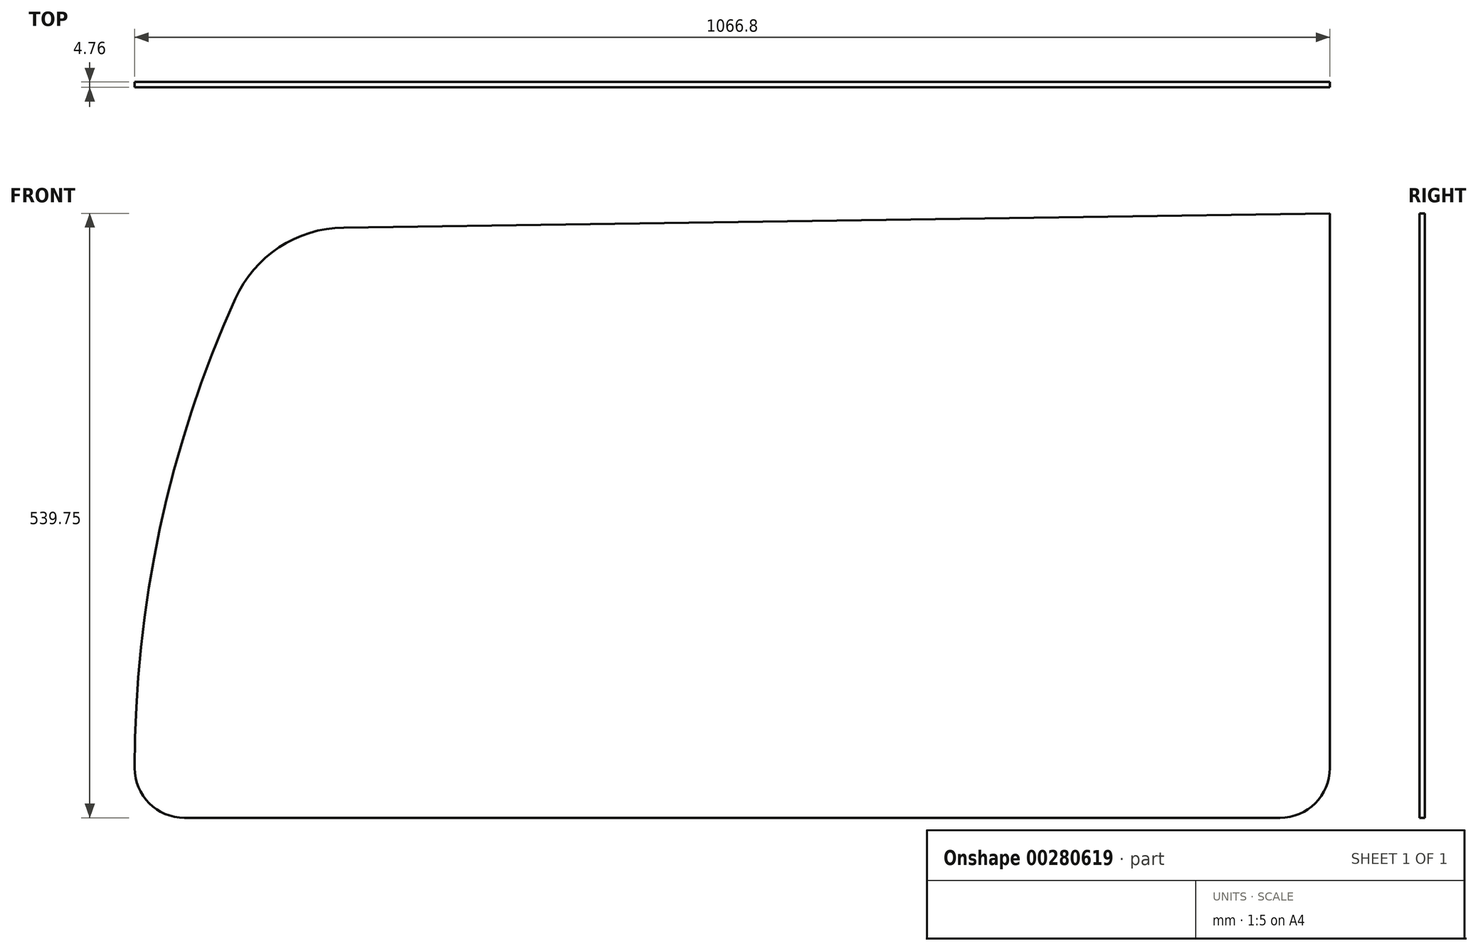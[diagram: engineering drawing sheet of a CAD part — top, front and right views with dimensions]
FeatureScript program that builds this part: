
annotation { "Feature Type Name" : "Feature", "Feature Type Description" : "" }
export const myFeature = defineFeature(function(context is Context, id is Id, definition is map)
    precondition{}
    {
        {
            var Q0;
            Q0=qCreatedBy(makeId("Front.planeOp"),FACE);
            var sketch = newSketch(context, id + "F0", { "sketchPlane" : qUnion([Q0])});
            skLineSegment(sketch, "E0", {"start": v(0, 44.45) * mm, "end": v(0, 539.75) * mm});
            skLineSegment(sketch, "E1", {"start": v(0, 539.75) * mm, "end": v(-880.13, 527.05) * mm});
            skLineSegment(sketch, "E2", {"start": v(-44.45, 0) * mm, "end": v(-1022.35, 0) * mm});
            skPoint(sketch, "E3.visualSharp", {"position": v(0, 0) * mm});
            skArc(sketch, "E3.filletArc", {"start": v(-44.45, 0) * mm, "mid": v(-13.02, 13.02) * mm, "end": v(0, 44.45) * mm});
            skArc(sketch, "E4", {"start": v(-880.13, 527.05) * mm, "mid": v(-937.87, 509.32) * mm, "end": v(-977.04, 463.34) * mm});
            skArc(sketch, "E5", {"start": v(-977.04, 463.34) * mm, "mid": v(-1044.1, 258.65) * mm, "end": v(-1066.8, 44.45) * mm});
            skArc(sketch, "E6", {"start": v(-1066.8, 44.45) * mm, "mid": v(-1053.78, 13.02) * mm, "end": v(-1022.35, 0) * mm});
            skSolve(sketch);
        }
        {
            var Q0;
            Q0=makeQuery(id+"F0.imprint","IMPRINT",FACE,{"disambiguationData":[TD([[makeQuery(id+"F0.imprint","IMPRINT",EDGE,{"derivedFrom":sQuery(id+"F0.wireOp",EDGE,"E0")}),1.0]])]});
            extrude(context, id + "F1", {"entities" : qUnion([Q0]), "depth" : 4.76 * mm});
        }
    });
